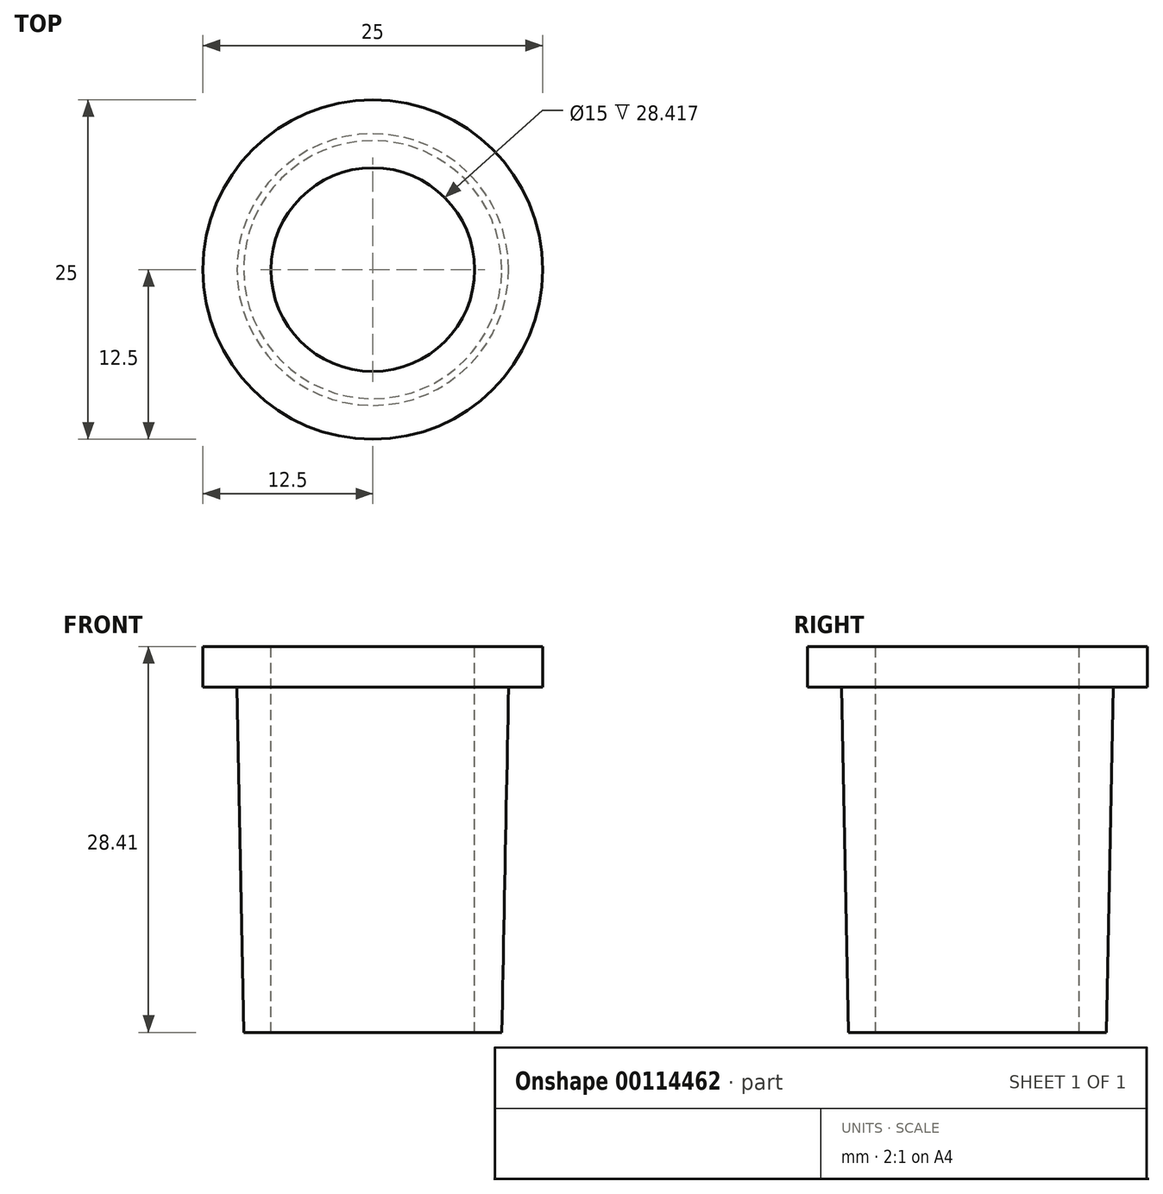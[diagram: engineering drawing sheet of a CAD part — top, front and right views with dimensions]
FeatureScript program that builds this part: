
annotation { "Feature Type Name" : "Feature", "Feature Type Description" : "" }
export const myFeature = defineFeature(function(context is Context, id is Id, definition is map)
    precondition{}
    {
        {
            var Q0;
            Q0=qCreatedBy(makeId("Right.planeOp"),FACE);
            var sketch = newSketch(context, id + "F0", { "sketchPlane" : qUnion([Q0])});
            skLineSegment(sketch, "E0", {"start": v(7.5, -18.21) * mm, "end": v(7.5, 10.2) * mm});
            skLineSegment(sketch, "E1", {"start": v(7.5, 10.2) * mm, "end": v(12.5, 10.2) * mm});
            skLineSegment(sketch, "E2", {"start": v(12.5, 10.2) * mm, "end": v(12.5, 7.2) * mm});
            skLineSegment(sketch, "E3", {"start": v(12.5, 7.2) * mm, "end": v(10, 7.2) * mm});
            skLineSegment(sketch, "E4", {"start": v(10, 7.2) * mm, "end": v(9.5, -18.21) * mm});
            skLineSegment(sketch, "E5", {"start": v(9.5, -18.21) * mm, "end": v(7.5, -18.21) * mm});
            skLineSegment(sketch, "E6", {"start": v(0, 14.05) * mm, "end": v(0, -21.7) * mm});
            skSolve(sketch);
        }
        {
            var Q0;
            Q0=makeQuery(id+"F0.imprint","IMPRINT",FACE,{"disambiguationData":[TD([[makeQuery(id+"F0.imprint","IMPRINT",EDGE,{"derivedFrom":sQuery(id+"F0.wireOp",EDGE,"E0")}),-1.0]])]});
            var Q1;
            Q1=sQuery(id+"F0.wireOp",EDGE,"E6");
            revolve(context, id + "F1", {"entities" : qUnion([Q0]), "axis" : qUnion([Q1]), "revolveType" : RevolveType.FULL});
        }
    });
